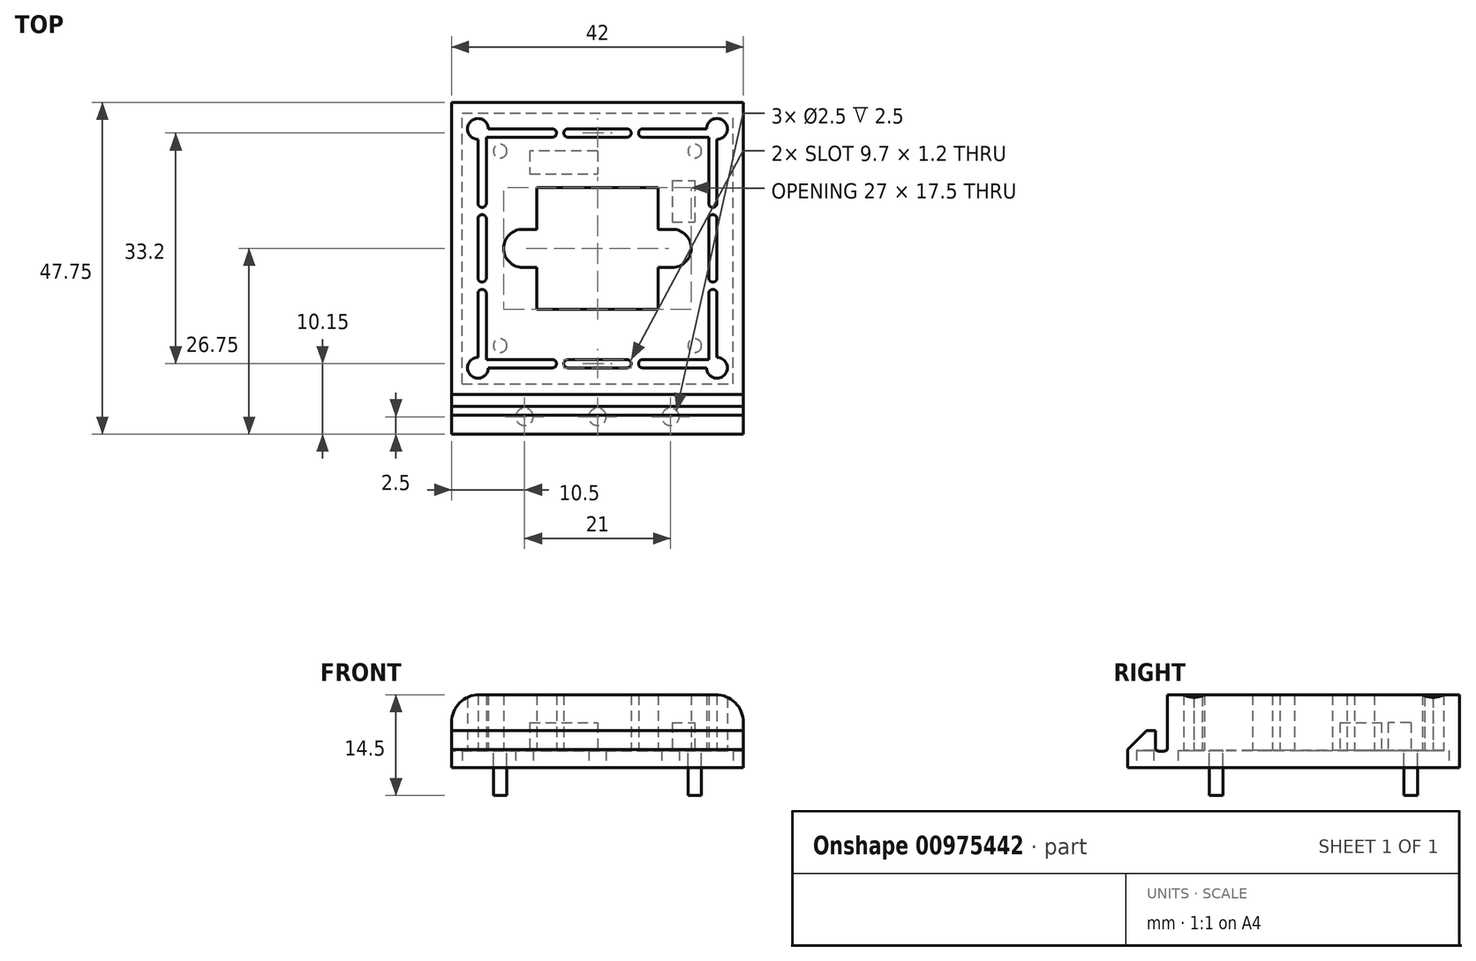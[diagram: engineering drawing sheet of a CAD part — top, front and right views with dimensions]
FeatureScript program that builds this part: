
annotation { "Feature Type Name" : "Feature", "Feature Type Description" : "" }
export const myFeature = defineFeature(function(context is Context, id is Id, definition is map)
    precondition{}
    {
        {
            var Q0;
            Q0=qCreatedBy(makeId("Top.planeOp"),FACE);
            var sketch = newSketch(context, id + "F0", { "sketchPlane" : qUnion([Q0])});
            skLineSegment(sketch, "E0.bottom", {"start": v(19, 19) * mm, "end": v(-19, 19) * mm, "construction": true});
            skLineSegment(sketch, "E0.top", {"start": v(19, -19) * mm, "end": v(-19, -19) * mm, "construction": true});
            skLineSegment(sketch, "E0.left", {"start": v(19, 19) * mm, "end": v(19, -19) * mm, "construction": true});
            skLineSegment(sketch, "E0.right", {"start": v(-19, 19) * mm, "end": v(-19, -19) * mm, "construction": true});
            skPoint(sketch, "E0.middle", {"position": v(0, 0) * mm});
            skPoint(sketch, "E1", {"position": v(19, 0) * mm});
            skPoint(sketch, "E2", {"position": v(-19, 0) * mm});
            skPoint(sketch, "E3", {"position": v(0, 19) * mm});
            skPoint(sketch, "E4", {"position": v(0, -19) * mm});
            skPoint(sketch, "E5", {"position": v(17.2, 0) * mm});
            skPoint(sketch, "E6", {"position": v(-17.2, 0) * mm});
            skLineSegment(sketch, "E7", {"start": v(-19, 0) * mm, "end": v(-17.2, 0) * mm, "construction": true});
            skLineSegment(sketch, "E8", {"start": v(19, 0) * mm, "end": v(17.2, 0) * mm, "construction": true});
            skLineSegment(sketch, "E9", {"start": v(0, 19) * mm, "end": v(0, 17.2) * mm, "construction": true});
            skLineSegment(sketch, "E10", {"start": v(0, -17.2) * mm, "end": v(0, -19) * mm, "construction": true});
            skPoint(sketch, "E11", {"position": v(-16, 16) * mm});
            skPoint(sketch, "E12", {"position": v(16, -16) * mm});
            skPoint(sketch, "E13", {"position": v(16, 16) * mm});
            skPoint(sketch, "E14", {"position": v(-16, -16) * mm});
            skPoint(sketch, "E15", {"position": v(17.2, 4.25) * mm});
            skPoint(sketch, "E16", {"position": v(17.2, -4.25) * mm});
            skPoint(sketch, "E17", {"position": v(16, -4.25) * mm});
            skPoint(sketch, "E18", {"position": v(16, 4.25) * mm});
            skPoint(sketch, "E19", {"position": v(-17.2, 4.25) * mm});
            skPoint(sketch, "E20", {"position": v(-16, 4.25) * mm});
            skPoint(sketch, "E21", {"position": v(-17.2, -4.25) * mm});
            skPoint(sketch, "E22", {"position": v(-16, -4.25) * mm});
            skPoint(sketch, "E23", {"position": v(-4.25, 17.2) * mm});
            skPoint(sketch, "E24", {"position": v(-4.25, 16) * mm});
            skPoint(sketch, "E25", {"position": v(4.25, 17.2) * mm});
            skPoint(sketch, "E26", {"position": v(4.25, 16) * mm});
            skPoint(sketch, "E27", {"position": v(-4.25, -16) * mm});
            skPoint(sketch, "E28", {"position": v(4.25, -16) * mm});
            skPoint(sketch, "E29", {"position": v(-4.25, -17.2) * mm});
            skPoint(sketch, "E30", {"position": v(4.25, -17.2) * mm});
            skLineSegment(sketch, "E31", {"start": v(17.2, 4.25) * mm, "end": v(17.2, -4.25) * mm});
            skLineSegment(sketch, "E32", {"start": v(16, 4.25) * mm, "end": v(16, -4.25) * mm});
            skLineSegment(sketch, "E33", {"start": v(4.25, 16) * mm, "end": v(-4.25, 16) * mm});
            skLineSegment(sketch, "E34", {"start": v(-4.25, 17.2) * mm, "end": v(4.25, 17.2) * mm});
            skLineSegment(sketch, "E35", {"start": v(-16, 4.25) * mm, "end": v(-16, -4.25) * mm});
            skLineSegment(sketch, "E36", {"start": v(-17.2, -4.25) * mm, "end": v(-17.2, 4.25) * mm});
            skLineSegment(sketch, "E37", {"start": v(-4.25, -16) * mm, "end": v(4.25, -16) * mm});
            skLineSegment(sketch, "E38", {"start": v(4.25, -17.2) * mm, "end": v(-4.25, -17.2) * mm});
            skArc(sketch, "E39", {"start": v(16, 4.25) * mm, "mid": v(16.6, 4.85) * mm, "end": v(17.2, 4.25) * mm});
            skArc(sketch, "E40", {"start": v(17.2, -4.25) * mm, "mid": v(16.6, -4.85) * mm, "end": v(16, -4.25) * mm});
            skArc(sketch, "E41", {"start": v(4.25, -16) * mm, "mid": v(4.85, -16.6) * mm, "end": v(4.25, -17.2) * mm});
            skArc(sketch, "E42", {"start": v(-4.25, -16) * mm, "mid": v(-4.85, -16.6) * mm, "end": v(-4.25, -17.2) * mm});
            skArc(sketch, "E43", {"start": v(-17.2, -4.25) * mm, "mid": v(-16.6, -4.85) * mm, "end": v(-16, -4.25) * mm});
            skArc(sketch, "E44", {"start": v(-17.2, 4.25) * mm, "mid": v(-16.6, 4.85) * mm, "end": v(-16, 4.25) * mm});
            skArc(sketch, "E45", {"start": v(-4.25, 16) * mm, "mid": v(-4.85, 16.6) * mm, "end": v(-4.25, 17.2) * mm});
            skArc(sketch, "E46", {"start": v(4.25, 16) * mm, "mid": v(4.85, 16.6) * mm, "end": v(4.25, 17.2) * mm});
            skPoint(sketch, "E47", {"position": v(-6.5, 16) * mm});
            skPoint(sketch, "E48", {"position": v(-6.5, 17.2) * mm});
            skPoint(sketch, "E49", {"position": v(-16, 6.5) * mm});
            skPoint(sketch, "E50", {"position": v(-17.2, 6.5) * mm});
            skPoint(sketch, "E51", {"position": v(6.5, 16) * mm});
            skPoint(sketch, "E52", {"position": v(6.5, 17.2) * mm});
            skPoint(sketch, "E53", {"position": v(16, 6.5) * mm});
            skPoint(sketch, "E54", {"position": v(17.2, 6.5) * mm});
            skPoint(sketch, "E55", {"position": v(-17.2, -6.5) * mm});
            skPoint(sketch, "E56", {"position": v(-16, -6.5) * mm});
            skPoint(sketch, "E57", {"position": v(17.2, -6.5) * mm});
            skPoint(sketch, "E58", {"position": v(16, -6.5) * mm});
            skPoint(sketch, "E59", {"position": v(6.5, -17.2) * mm});
            skPoint(sketch, "E60", {"position": v(6.5, -16) * mm});
            skPoint(sketch, "E61", {"position": v(-6.5, -17.2) * mm});
            skPoint(sketch, "E62", {"position": v(-6.5, -16) * mm});
            skLineSegment(sketch, "E63", {"start": v(-6.5, 17.2) * mm, "end": v(-6.5, 16) * mm, "construction": true});
            skLineSegment(sketch, "E64", {"start": v(-17.2, 6.5) * mm, "end": v(-16, 6.5) * mm, "construction": true});
            skLineSegment(sketch, "E65", {"start": v(6.5, 17.2) * mm, "end": v(6.5, 16) * mm, "construction": true});
            skLineSegment(sketch, "E66", {"start": v(16, 6.5) * mm, "end": v(17.2, 6.5) * mm, "construction": true});
            skLineSegment(sketch, "E67", {"start": v(-17.2, -6.5) * mm, "end": v(-16, -6.5) * mm, "construction": true});
            skLineSegment(sketch, "E68", {"start": v(-6.5, -16) * mm, "end": v(-6.5, -17.2) * mm, "construction": true});
            skLineSegment(sketch, "E69", {"start": v(16, -6.5) * mm, "end": v(17.2, -6.5) * mm, "construction": true});
            skLineSegment(sketch, "E70", {"start": v(6.5, -16) * mm, "end": v(6.5, -17.2) * mm, "construction": true});
            skArc(sketch, "E71", {"start": v(-6.5, 17.2) * mm, "mid": v(-5.9, 16.6) * mm, "end": v(-6.5, 16) * mm});
            skArc(sketch, "E72", {"start": v(-16, 6.5) * mm, "mid": v(-16.6, 5.9) * mm, "end": v(-17.2, 6.5) * mm});
            skArc(sketch, "E73", {"start": v(6.5, 17.2) * mm, "mid": v(5.9, 16.6) * mm, "end": v(6.5, 16) * mm});
            skArc(sketch, "E74", {"start": v(17.2, 6.5) * mm, "mid": v(16.6, 5.9) * mm, "end": v(16, 6.5) * mm});
            skArc(sketch, "E75", {"start": v(-16, -6.5) * mm, "mid": v(-16.6, -5.9) * mm, "end": v(-17.2, -6.5) * mm});
            skArc(sketch, "E76", {"start": v(-6.5, -16) * mm, "mid": v(-5.9, -16.6) * mm, "end": v(-6.5, -17.2) * mm});
            skArc(sketch, "E77", {"start": v(6.5, -16) * mm, "mid": v(5.9, -16.6) * mm, "end": v(6.5, -17.2) * mm});
            skArc(sketch, "E78", {"start": v(17.2, -6.5) * mm, "mid": v(16.6, -5.9) * mm, "end": v(16, -6.5) * mm});
            skLineSegment(sketch, "E79", {"start": v(6.5, 17.2) * mm, "end": v(16, 17.2) * mm});
            skLineSegment(sketch, "E80", {"start": v(6.5, 16) * mm, "end": v(16, 16) * mm});
            skLineSegment(sketch, "E81", {"start": v(16, 6.5) * mm, "end": v(16, 16) * mm});
            skLineSegment(sketch, "E82", {"start": v(17.2, 16) * mm, "end": v(17.2, 6.5) * mm});
            skLineSegment(sketch, "E83", {"start": v(-16, 17.2) * mm, "end": v(-6.5, 17.2) * mm});
            skLineSegment(sketch, "E84", {"start": v(-16, 16) * mm, "end": v(-6.5, 16) * mm});
            skLineSegment(sketch, "E85", {"start": v(-16, 16) * mm, "end": v(-16, 6.5) * mm});
            skLineSegment(sketch, "E86", {"start": v(-17.2, 6.5) * mm, "end": v(-17.2, 16) * mm});
            skLineSegment(sketch, "E87", {"start": v(-16, -6.5) * mm, "end": v(-16, -16) * mm});
            skLineSegment(sketch, "E88", {"start": v(-6.5, -16) * mm, "end": v(-16, -16) * mm});
            skLineSegment(sketch, "E89", {"start": v(-17.2, -6.5) * mm, "end": v(-17.2, -16) * mm});
            skLineSegment(sketch, "E90", {"start": v(-16, -17.2) * mm, "end": v(-6.5, -17.2) * mm});
            skLineSegment(sketch, "E91", {"start": v(6.5, -17.2) * mm, "end": v(16, -17.2) * mm});
            skLineSegment(sketch, "E92", {"start": v(6.5, -16) * mm, "end": v(16, -16) * mm});
            skLineSegment(sketch, "E93", {"start": v(17.2, -16) * mm, "end": v(17.2, -6.5) * mm});
            skLineSegment(sketch, "E94", {"start": v(16, -6.5) * mm, "end": v(16, -16) * mm});
            skLineSegment(sketch, "E95", {"start": v(-17.2, 6.5) * mm, "end": v(-19, 6.5) * mm, "construction": true});
            skLineSegment(sketch, "E96", {"start": v(-17.2, -6.5) * mm, "end": v(-19, -6.5) * mm, "construction": true});
            skLineSegment(sketch, "E97", {"start": v(-6.5, 17.2) * mm, "end": v(-6.5, 19) * mm, "construction": true});
            skLineSegment(sketch, "E98", {"start": v(-6.5, -17.2) * mm, "end": v(-6.5, -19) * mm, "construction": true});
            skLineSegment(sketch, "E99", {"start": v(6.5, -17.2) * mm, "end": v(6.5, -19) * mm, "construction": true});
            skLineSegment(sketch, "E100", {"start": v(17.2, -6.5) * mm, "end": v(19, -6.5) * mm, "construction": true});
            skLineSegment(sketch, "E101", {"start": v(17.2, 6.5) * mm, "end": v(19, 6.5) * mm, "construction": true});
            skLineSegment(sketch, "E102", {"start": v(6.5, 17.2) * mm, "end": v(6.5, 19) * mm, "construction": true});
            skPoint(sketch, "E103", {"position": v(-11.25, 17.2) * mm});
            skPoint(sketch, "E104", {"position": v(-11.25, 16) * mm});
            skPoint(sketch, "E105", {"position": v(-17.2, 11.25) * mm});
            skPoint(sketch, "E106", {"position": v(-16, 11.25) * mm});
            skPoint(sketch, "E107", {"position": v(11.25, 17.2) * mm});
            skPoint(sketch, "E108", {"position": v(11.25, 16) * mm});
            skPoint(sketch, "E109", {"position": v(16, 11.25) * mm});
            skPoint(sketch, "E110", {"position": v(17.2, 11.25) * mm});
            skPoint(sketch, "E111", {"position": v(16, -11.25) * mm});
            skPoint(sketch, "E112", {"position": v(17.2, -11.25) * mm});
            skPoint(sketch, "E113", {"position": v(11.25, -16) * mm});
            skPoint(sketch, "E114", {"position": v(11.25, -17.2) * mm});
            skPoint(sketch, "E115", {"position": v(-11.25, -16) * mm});
            skPoint(sketch, "E116", {"position": v(-11.25, -17.2) * mm});
            skPoint(sketch, "E117", {"position": v(-16, -11.25) * mm});
            skPoint(sketch, "E118", {"position": v(-17.2, -11.25) * mm});
            skLineSegment(sketch, "E119", {"start": v(-17.2, 11.25) * mm, "end": v(-16, 11.25) * mm, "construction": true});
            skLineSegment(sketch, "E120", {"start": v(-11.25, 17.2) * mm, "end": v(-11.25, 16) * mm, "construction": true});
            skLineSegment(sketch, "E121", {"start": v(-11.25, -16) * mm, "end": v(-11.25, -17.2) * mm, "construction": true});
            skLineSegment(sketch, "E122", {"start": v(-16, -11.25) * mm, "end": v(-17.2, -11.25) * mm, "construction": true});
            skLineSegment(sketch, "E123", {"start": v(11.25, 17.2) * mm, "end": v(11.25, 16) * mm, "construction": true});
            skLineSegment(sketch, "E124", {"start": v(16, 11.25) * mm, "end": v(17.2, 11.25) * mm, "construction": true});
            skLineSegment(sketch, "E125", {"start": v(11.25, -17.2) * mm, "end": v(11.25, -16) * mm, "construction": true});
            skLineSegment(sketch, "E126", {"start": v(16, -11.25) * mm, "end": v(17.2, -11.25) * mm, "construction": true});
            skPoint(sketch, "E127", {"position": v(-14, 14) * mm});
            skLineSegment(sketch, "E128", {"start": v(-14, 19) * mm, "end": v(-14, 14) * mm, "construction": true});
            skLineSegment(sketch, "E129", {"start": v(-14, 14) * mm, "end": v(-19, 14) * mm, "construction": true});
            skPoint(sketch, "E130", {"position": v(-14, -14) * mm});
            skLineSegment(sketch, "E131", {"start": v(-19, -14) * mm, "end": v(-14, -14) * mm, "construction": true});
            skLineSegment(sketch, "E132", {"start": v(-14, -19) * mm, "end": v(-14, -14) * mm, "construction": true});
            skPoint(sketch, "E133", {"position": v(14, -14) * mm});
            skLineSegment(sketch, "E134", {"start": v(14, -19) * mm, "end": v(14, -14) * mm, "construction": true});
            skLineSegment(sketch, "E135", {"start": v(14, -14) * mm, "end": v(19, -14) * mm, "construction": true});
            skPoint(sketch, "E136", {"position": v(14, 14) * mm});
            skLineSegment(sketch, "E137", {"start": v(14, 19) * mm, "end": v(14, 14) * mm, "construction": true});
            skLineSegment(sketch, "E138", {"start": v(19, 14) * mm, "end": v(14, 14) * mm, "construction": true});
            skPoint(sketch, "E139", {"position": v(16, 0) * mm});
            skPoint(sketch, "E140", {"position": v(0, 16) * mm});
            skPoint(sketch, "E141", {"position": v(-16, 0) * mm});
            skPoint(sketch, "E142", {"position": v(0, -16) * mm});
            skLineSegment(sketch, "E143", {"start": v(16, 0) * mm, "end": v(17.2, 0) * mm, "construction": true});
            skLineSegment(sketch, "E144", {"start": v(0, 17.2) * mm, "end": v(0, 16) * mm, "construction": true});
            skLineSegment(sketch, "E145", {"start": v(0, -16) * mm, "end": v(0, -17.2) * mm, "construction": true});
            skLineSegment(sketch, "E146", {"start": v(-17.2, 0) * mm, "end": v(-16, 0) * mm, "construction": true});
            skPoint(sketch, "E147", {"position": v(-17.2, 17.2) * mm});
            skPoint(sketch, "E148", {"position": v(17.2, 17.2) * mm});
            skPoint(sketch, "E149", {"position": v(-17.2, -17.2) * mm});
            skPoint(sketch, "E150", {"position": v(17.2, -17.2) * mm});
            skLineSegment(sketch, "E151", {"start": v(16, 4.25) * mm, "end": v(17.2, 4.25) * mm, "construction": true});
            skLineSegment(sketch, "E152", {"start": v(16, -4.25) * mm, "end": v(17.2, -4.25) * mm, "construction": true});
            skLineSegment(sketch, "E153", {"start": v(-4.25, 16) * mm, "end": v(-4.25, 17.2) * mm, "construction": true});
            skLineSegment(sketch, "E154", {"start": v(4.25, 16) * mm, "end": v(4.25, 17.2) * mm, "construction": true});
            skLineSegment(sketch, "E155", {"start": v(-16, 4.25) * mm, "end": v(-17.2, 4.25) * mm, "construction": true});
            skLineSegment(sketch, "E156", {"start": v(-16, -4.25) * mm, "end": v(-17.2, -4.25) * mm, "construction": true});
            skLineSegment(sketch, "E157", {"start": v(-4.25, -16) * mm, "end": v(-4.25, -17.2) * mm, "construction": true});
            skLineSegment(sketch, "E158", {"start": v(4.25, -16) * mm, "end": v(4.25, -17.2) * mm, "construction": true});
            skLineSegment(sketch, "E159", {"start": v(-6.5, 17.2) * mm, "end": v(-4.25, 17.2) * mm, "construction": true});
            skLineSegment(sketch, "E160", {"start": v(4.25, 17.2) * mm, "end": v(6.5, 17.2) * mm, "construction": true});
            skLineSegment(sketch, "E161", {"start": v(17.2, 6.5) * mm, "end": v(17.2, 4.25) * mm, "construction": true});
            skLineSegment(sketch, "E162", {"start": v(17.2, -6.5) * mm, "end": v(17.2, -4.25) * mm, "construction": true});
            skLineSegment(sketch, "E163", {"start": v(6.5, -17.2) * mm, "end": v(4.25, -17.2) * mm, "construction": true});
            skLineSegment(sketch, "E164", {"start": v(-4.25, -17.2) * mm, "end": v(-6.5, -17.2) * mm, "construction": true});
            skLineSegment(sketch, "E165", {"start": v(-17.2, -6.5) * mm, "end": v(-17.2, -4.25) * mm, "construction": true});
            skLineSegment(sketch, "E166", {"start": v(-17.2, 4.25) * mm, "end": v(-17.2, 6.5) * mm, "construction": true});
            skCircle(sketch, "E167", {"center": v(14, 14) * mm, "radius": 0.97 * mm});
            skPoint(sketch, "E168", {"position": v(14, 14.97) * mm});
            skPoint(sketch, "E169", {"position": v(14.97, 14) * mm});
            skPoint(sketch, "E170", {"position": v(16, 14) * mm});
            skPoint(sketch, "E171", {"position": v(14, 16) * mm});
            skCircle(sketch, "E172", {"center": v(-14, 14) * mm, "radius": 0.97 * mm});
            skPoint(sketch, "E173", {"position": v(-14, 14.97) * mm});
            skPoint(sketch, "E174", {"position": v(-14.97, 14) * mm});
            skCircle(sketch, "E175", {"center": v(-14, -14) * mm, "radius": 0.97 * mm});
            skCircle(sketch, "E176", {"center": v(14, -14) * mm, "radius": 0.97 * mm});
            skPoint(sketch, "E177", {"position": v(14, -14.97) * mm});
            skPoint(sketch, "E178", {"position": v(14.97, -14) * mm});
            skPoint(sketch, "E179", {"position": v(-14.97, -14) * mm});
            skPoint(sketch, "E180", {"position": v(-14, -14.97) * mm});
            skLineSegment(sketch, "E181.bottom", {"start": v(8.75, 8.75) * mm, "end": v(-8.75, 8.75) * mm});
            skLineSegment(sketch, "E181.top", {"start": v(8.75, -8.75) * mm, "end": v(-8.75, -8.75) * mm});
            skLineSegment(sketch, "E181.left", {"start": v(8.75, 8.75) * mm, "end": v(8.75, 2.75) * mm});
            skLineSegment(sketch, "E181.right", {"start": v(-8.75, 8.75) * mm, "end": v(-8.75, 2.75) * mm});
            skLineSegment(sketch, "E182.bottom", {"start": v(-21, 21) * mm, "end": v(-2.62, 21) * mm});
            skLineSegment(sketch, "E182.top", {"start": v(-21, -21) * mm, "end": v(-2.63, -21) * mm});
            skLineSegment(sketch, "E182.left", {"start": v(-21, 21) * mm, "end": v(-21, -21) * mm});
            skLineSegment(sketch, "E182.right", {"start": v(21, 21) * mm, "end": v(21, -21) * mm});
            skPoint(sketch, "E183", {"position": v(0, 21) * mm});
            skPoint(sketch, "E184", {"position": v(-2.62, 21) * mm});
            skPoint(sketch, "E185", {"position": v(2.62, 21) * mm});
            skLineSegment(sketch, "E186.trimOffspring", {"start": v(2.62, 21) * mm, "end": v(21, 21) * mm});
            skPoint(sketch, "E187", {"position": v(0, -21) * mm});
            skPoint(sketch, "E188", {"position": v(-2.63, -21) * mm});
            skPoint(sketch, "E189", {"position": v(2.63, -21) * mm});
            skLineSegment(sketch, "E190.trimOffspring", {"start": v(2.63, -21) * mm, "end": v(21, -21) * mm});
            skLineSegment(sketch, "E191", {"start": v(-2.62, 21) * mm, "end": v(2.63, 21) * mm});
            skLineSegment(sketch, "E192", {"start": v(-2.63, -21) * mm, "end": v(2.63, -21) * mm});
            skPoint(sketch, "E193", {"position": v(-8.75, 0) * mm});
            skPoint(sketch, "E194", {"position": v(8.75, 0) * mm});
            skPoint(sketch, "E195", {"position": v(8.75, -2.75) * mm});
            skPoint(sketch, "E196", {"position": v(8.75, 2.75) * mm});
            skPoint(sketch, "E197", {"position": v(-8.75, -2.75) * mm});
            skPoint(sketch, "E198", {"position": v(-8.75, 2.75) * mm});
            skLineSegment(sketch, "E199", {"start": v(-8.75, -2.75) * mm, "end": v(8.75, -2.75) * mm, "construction": true});
            skLineSegment(sketch, "E200", {"start": v(8.75, 2.75) * mm, "end": v(-8.75, 2.75) * mm, "construction": true});
            skPoint(sketch, "E201", {"position": v(10.75, 0) * mm});
            skPoint(sketch, "E202", {"position": v(-10.75, 0) * mm});
            skLineSegment(sketch, "E203", {"start": v(10.75, 0) * mm, "end": v(8.75, 0) * mm, "construction": true});
            skLineSegment(sketch, "E204", {"start": v(-10.75, 0) * mm, "end": v(-8.75, 0) * mm, "construction": true});
            skLineSegment(sketch, "E205", {"start": v(-8.75, -2.75) * mm, "end": v(-10.75, -2.75) * mm});
            skLineSegment(sketch, "E206", {"start": v(-8.75, 2.75) * mm, "end": v(-10.75, 2.75) * mm});
            skLineSegment(sketch, "E207", {"start": v(8.75, -2.75) * mm, "end": v(10.75, -2.75) * mm});
            skLineSegment(sketch, "E208", {"start": v(8.75, 2.75) * mm, "end": v(10.75, 2.75) * mm});
            skArc(sketch, "E209", {"start": v(-10.75, 2.75) * mm, "mid": v(-13.5, 0) * mm, "end": v(-10.75, -2.75) * mm});
            skArc(sketch, "E210", {"start": v(10.75, -2.75) * mm, "mid": v(13.5, 0) * mm, "end": v(10.75, 2.75) * mm});
            skLineSegment(sketch, "E211.trimOffspring", {"start": v(-8.75, -2.75) * mm, "end": v(-8.75, -8.75) * mm});
            skLineSegment(sketch, "E212.trimOffspring", {"start": v(8.75, -2.75) * mm, "end": v(8.75, -8.75) * mm});
            skLineSegment(sketch, "E213", {"start": v(-16, -6.5) * mm, "end": v(-16, -4.25) * mm});
            skLineSegment(sketch, "E214", {"start": v(-16, 4.25) * mm, "end": v(-16, 6.5) * mm});
            skLineSegment(sketch, "E215", {"start": v(-6.5, -16) * mm, "end": v(-4.25, -16) * mm});
            skLineSegment(sketch, "E216", {"start": v(4.25, -16) * mm, "end": v(6.5, -16) * mm});
            skLineSegment(sketch, "E217", {"start": v(16, -4.25) * mm, "end": v(16, -6.5) * mm});
            skLineSegment(sketch, "E218", {"start": v(16, 4.25) * mm, "end": v(16, 6.5) * mm});
            skLineSegment(sketch, "E219", {"start": v(6.5, 16) * mm, "end": v(4.25, 16) * mm});
            skLineSegment(sketch, "E220", {"start": v(-4.25, 16) * mm, "end": v(-6.5, 16) * mm});
            skArc(sketch, "E221", {"start": v(-15.7, 17.2) * mm, "mid": v(-18.26, 18.26) * mm, "end": v(-17.2, 15.7) * mm});
            skLineSegment(sketch, "E222", {"start": v(-17.2, 16) * mm, "end": v(-17.2, 17.2) * mm, "construction": true});
            skLineSegment(sketch, "E223", {"start": v(-17.2, 17.2) * mm, "end": v(-17.2, 19) * mm, "construction": true});
            skLineSegment(sketch, "E224", {"start": v(-16, 17.2) * mm, "end": v(-17.2, 17.2) * mm, "construction": true});
            skLineSegment(sketch, "E225", {"start": v(-17.2, 17.2) * mm, "end": v(-19, 17.2) * mm, "construction": true});
            skArc(sketch, "E226", {"start": v(17.2, 15.7) * mm, "mid": v(18.26, 18.26) * mm, "end": v(15.7, 17.2) * mm});
            skLineSegment(sketch, "E227", {"start": v(16, 17.2) * mm, "end": v(17.2, 17.2) * mm, "construction": true});
            skLineSegment(sketch, "E228", {"start": v(17.2, 16) * mm, "end": v(17.2, 17.2) * mm, "construction": true});
            skLineSegment(sketch, "E229", {"start": v(17.2, 17.2) * mm, "end": v(17.2, 19) * mm, "construction": true});
            skLineSegment(sketch, "E230", {"start": v(17.2, 17.2) * mm, "end": v(19, 17.2) * mm, "construction": true});
            skArc(sketch, "E231", {"start": v(-17.2, -15.7) * mm, "mid": v(-18.26, -18.26) * mm, "end": v(-15.7, -17.2) * mm});
            skArc(sketch, "E232", {"start": v(15.7, -17.2) * mm, "mid": v(18.26, -18.26) * mm, "end": v(17.2, -15.7) * mm});
            skLineSegment(sketch, "E233", {"start": v(17.2, -16) * mm, "end": v(17.2, -17.2) * mm, "construction": true});
            skLineSegment(sketch, "E234", {"start": v(17.2, -17.2) * mm, "end": v(17.2, -19) * mm, "construction": true});
            skLineSegment(sketch, "E235", {"start": v(16, -17.2) * mm, "end": v(17.2, -17.2) * mm, "construction": true});
            skLineSegment(sketch, "E236", {"start": v(17.2, -17.2) * mm, "end": v(19, -17.2) * mm, "construction": true});
            skLineSegment(sketch, "E237", {"start": v(-17.2, -16) * mm, "end": v(-17.2, -17.2) * mm, "construction": true});
            skLineSegment(sketch, "E238", {"start": v(-17.2, -17.2) * mm, "end": v(-17.2, -19) * mm, "construction": true});
            skLineSegment(sketch, "E239", {"start": v(-16, -17.2) * mm, "end": v(-17.2, -17.2) * mm, "construction": true});
            skLineSegment(sketch, "E240", {"start": v(-17.2, -17.2) * mm, "end": v(-19, -17.2) * mm, "construction": true});
            skPoint(sketch, "E241", {"position": v(15.7, 17.2) * mm});
            skPoint(sketch, "E242", {"position": v(17.2, 15.7) * mm});
            skPoint(sketch, "E243", {"position": v(-17.2, 15.7) * mm});
            skPoint(sketch, "E244", {"position": v(-15.7, 17.2) * mm});
            skPoint(sketch, "E245", {"position": v(-17.2, -15.7) * mm});
            skPoint(sketch, "E246", {"position": v(-15.7, -17.2) * mm});
            skPoint(sketch, "E247", {"position": v(15.7, -17.2) * mm});
            skPoint(sketch, "E248", {"position": v(17.2, -15.7) * mm});
            skLineSegment(sketch, "E249.bottom", {"start": v(-19.5, -19.5) * mm, "end": v(19.5, -19.5) * mm});
            skLineSegment(sketch, "E249.top", {"start": v(-19.5, 19.5) * mm, "end": v(19.5, 19.5) * mm});
            skLineSegment(sketch, "E249.left", {"start": v(-19.5, -19.5) * mm, "end": v(-19.5, 19.5) * mm});
            skLineSegment(sketch, "E249.right", {"start": v(19.5, -19.5) * mm, "end": v(19.5, 19.5) * mm});
            skPoint(sketch, "E250", {"position": v(-8.75, 10.75) * mm});
            skPoint(sketch, "E251", {"position": v(-8.75, 14) * mm});
            skPoint(sketch, "E252", {"position": v(0, 8.75) * mm});
            skPoint(sketch, "E253", {"position": v(0, 10.75) * mm});
            skPoint(sketch, "E254", {"position": v(0, 14) * mm});
            skLineSegment(sketch, "E255", {"start": v(0, 14) * mm, "end": v(0, 10.75) * mm});
            skLineSegment(sketch, "E256", {"start": v(-8.75, 10.75) * mm, "end": v(0, 10.75) * mm});
            skLineSegment(sketch, "E257", {"start": v(0, 14) * mm, "end": v(-8.75, 14) * mm});
            skLineSegment(sketch, "E258", {"start": v(-8.75, 14) * mm, "end": v(-9.75, 14) * mm});
            skLineSegment(sketch, "E259", {"start": v(-9.75, 14) * mm, "end": v(-9.75, 10.75) * mm});
            skLineSegment(sketch, "E260", {"start": v(-9.75, 10.75) * mm, "end": v(-8.75, 10.75) * mm});
            skPoint(sketch, "E261", {"position": v(10.75, 8.75) * mm});
            skPoint(sketch, "E262", {"position": v(14, 8.75) * mm});
            skLineSegment(sketch, "E263", {"start": v(10.75, 8.75) * mm, "end": v(10.75, 3.81) * mm});
            skLineSegment(sketch, "E264", {"start": v(10.75, 3.81) * mm, "end": v(14, 3.81) * mm});
            skLineSegment(sketch, "E265", {"start": v(14, 3.81) * mm, "end": v(14, 8.75) * mm});
            skLineSegment(sketch, "E266", {"start": v(10.75, 8.75) * mm, "end": v(10.75, 9.75) * mm});
            skLineSegment(sketch, "E267", {"start": v(10.75, 9.75) * mm, "end": v(14, 9.75) * mm});
            skLineSegment(sketch, "E268", {"start": v(14, 9.75) * mm, "end": v(14, 8.75) * mm});
            skSolve(sketch);
        }
        {
            var Q0;
            Q0=qSketchRegion(id+"F0",true);
            var Q1;
            Q1=makeQuery(id+"F0.imprint","IMPRINT",FACE,{"disambiguationData":[TD([[makeQuery(id+"F0.imprint","IMPRINT",EDGE,{"derivedFrom":sQuery(id+"F0.wireOp",EDGE,"E176")}),1.0]])]});
            var Q2;
            Q2=makeQuery(id+"F0.imprint","IMPRINT",FACE,{"disambiguationData":[TD([[makeQuery(id+"F0.imprint","IMPRINT",EDGE,{"derivedFrom":sQuery(id+"F0.wireOp",EDGE,"E175")}),1.0]])]});
            var Q3;
            Q3=makeQuery(id+"F0.imprint","IMPRINT",FACE,{"disambiguationData":[TD([[makeQuery(id+"F0.imprint","IMPRINT",EDGE,{"derivedFrom":sQuery(id+"F0.wireOp",EDGE,"E172")}),1.0]])]});
            var Q4;
            Q4=makeQuery(id+"F0.imprint","IMPRINT",FACE,{"disambiguationData":[TD([[makeQuery(id+"F0.imprint","IMPRINT",EDGE,{"derivedFrom":sQuery(id+"F0.wireOp",EDGE,"E167")}),1.0]])]});
            var Q5;
            Q5=makeQuery(id+"F0.imprint","IMPRINT",FACE,{"disambiguationData":[TD([[makeQuery(id+"F0.imprint","IMPRINT",EDGE,{"derivedFrom":sQuery(id+"F0.wireOp",EDGE,"E32")}),-1.0]])]});
            var Q6;
            Q6=makeQuery(id+"F0.imprint","IMPRINT",FACE,{"disambiguationData":[TD([[makeQuery(id+"F0.imprint","IMPRINT",EDGE,{"derivedFrom":sQuery(id+"F0.wireOp",EDGE,"E31")}),1.0]])]});
            var Q7;
            Q7=makeQuery(id+"F0.imprint","IMPRINT",FACE,{"disambiguationData":[TD([[makeQuery(id+"F0.imprint","IMPRINT",EDGE,{"derivedFrom":sQuery(id+"F0.wireOp",EDGE,"E263")}),1.0]])]});
            var Q8;
            Q8=makeQuery(id+"F0.imprint","IMPRINT",FACE,{"disambiguationData":[TD([[makeQuery(id+"F0.imprint","IMPRINT",EDGE,{"derivedFrom":sQuery(id+"F0.wireOp",EDGE,"E255")}),-1.0]])]});
            extrude(context, id + "F1", {"entities" : qUnion([Q0, Q1, Q2, Q3, Q4, Q5, Q6, Q7, Q8]), "depth" : 9 * mm, "offsetDistance" : 25 * mm});
        }
        {
            var Q0;
            Q0=makeQuery(id+"F1.opExtrude","CAP_EDGE",EDGE,{"disambiguationData":[OSD([sQuery(id+"F0.wireOp",EDGE,"E182.left")])],"isStart":false});
            var Q1;
            Q1=makeQuery(id+"F1.opExtrude","CAP_EDGE",EDGE,{"disambiguationData":[OSD([sQuery(id+"F0.wireOp",EDGE,"E182.right")])],"isStart":false});
            fillet(context, id + "F2", {"entities" : qUnion([Q0, Q1]), "radius" : 4 * mm, "tangentPropagation" : true, "allowEdgeOverflow" : false});
        }
        {
            var Q0;
            Q0=qCreatedBy(makeId("Right.planeOp"),FACE);
            var sketch = newSketch(context, id + "F3", { "sketchPlane" : qUnion([Q0])});
            skLineSegment(sketch, "E269", {"start": v(-21, 1.1) * mm, "end": v(-21, 0) * mm});
            skLineSegment(sketch, "E270", {"start": v(-21, 0) * mm, "end": v(-21, -1.5) * mm});
            skLineSegment(sketch, "E271", {"start": v(-21, -1.5) * mm, "end": v(-22.75, -1.5) * mm});
            skLineSegment(sketch, "E272", {"start": v(-21, 1.1) * mm, "end": v(-22.75, 1.1) * mm, "construction": true});
            skLineSegment(sketch, "E273", {"start": v(-22.75, 1.1) * mm, "end": v(-22.75, -1.5) * mm, "construction": true});
            skLineSegment(sketch, "E274", {"start": v(-22.75, 1.1) * mm, "end": v(-22.75, 3.85) * mm});
            skLineSegment(sketch, "E275", {"start": v(-22.75, 3.85) * mm, "end": v(-24, 3.85) * mm});
            skLineSegment(sketch, "E276", {"start": v(-24, 3.85) * mm, "end": v(-26.75, 1.1) * mm});
            skLineSegment(sketch, "E277", {"start": v(-26.75, 1.1) * mm, "end": v(-26.75, -1.5) * mm});
            skLineSegment(sketch, "E278", {"start": v(-26.75, -1.5) * mm, "end": v(-22.75, -1.5) * mm});
            skArc(sketch, "E279", {"start": v(-22.75, 1.1) * mm, "mid": v(-21.88, 0.82) * mm, "end": v(-21, 1.1) * mm});
            skSolve(sketch);
        }
        {
            var Q0;
            Q0=qSketchRegion(id+"F3",true);
            extrude(context, id + "F4", {"entities" : qUnion([Q0]), "operationType" : NewBodyOperationType.ADD, "depth" : 21 * mm, "offsetDistance" : 25 * mm});
        }
        {
            var Q0;
            Q0=makeQuery(id+"F4.opExtrude","CAP_FACE",FACE,{"disambiguationData":[OSD([sQuery(id+"F3.wireOp",EDGE,"W3A2iIaU-WZcM-LwCZ-avBC-8jkScGPnRnPX"),sQuery(id+"F3.wireOp",EDGE,"ALWewPtL-lRdy-D1S6-Pmp3-0LCmG40DPnmF"),sQuery(id+"F3.wireOp",EDGE,"E269"),sQuery(id+"F3.wireOp",EDGE,"a8HGcZms-0psD-ubHa-zhNr-YMWZytVFjQNi"),sQuery(id+"F3.wireOp",EDGE,"o8Ebxgyn-Q84Y-cI0J-CGKw-LX74F4kokC7l"),sQuery(id+"F3.wireOp",EDGE,"YJE5rnin-kTqy-YI2g-DbKN-iJDOnxPtUyyk"),sQuery(id+"F3.wireOp",EDGE,"J2bwKcV5-MZwX-Vs9f-UurF-KyFTJAMSioa0"),sQuery(id+"F3.wireOp",EDGE,"OojeKQKz-hSKq-U6jK-n3HU-CNnbXeyMiDCb")])],"isStart":true});
            extrude(context, id + "F5", {"entities" : qUnion([Q0]), "operationType" : NewBodyOperationType.ADD, "depth" : 21 * mm, "offsetDistance" : 25 * mm});
        }
        {
            var Q0;
            Q0=makeQuery(id+"F0.imprint","IMPRINT",FACE,{"disambiguationData":[TD([[makeQuery(id+"F0.imprint","IMPRINT",EDGE,{"derivedFrom":sQuery(id+"F0.wireOp",EDGE,"E175")}),1.0]])]});
            var Q1;
            Q1=makeQuery(id+"F0.imprint","IMPRINT",FACE,{"disambiguationData":[TD([[makeQuery(id+"F0.imprint","IMPRINT",EDGE,{"derivedFrom":sQuery(id+"F0.wireOp",EDGE,"E176")}),1.0]])]});
            var Q2;
            Q2=makeQuery(id+"F0.imprint","IMPRINT",FACE,{"disambiguationData":[TD([[makeQuery(id+"F0.imprint","IMPRINT",EDGE,{"derivedFrom":sQuery(id+"F0.wireOp",EDGE,"E172")}),1.0]])]});
            var Q3;
            Q3=makeQuery(id+"F0.imprint","IMPRINT",FACE,{"disambiguationData":[TD([[makeQuery(id+"F0.imprint","IMPRINT",EDGE,{"derivedFrom":sQuery(id+"F0.wireOp",EDGE,"E167")}),1.0]])]});
            var Q4;
            Q4=sQuery(id+"F0.wireOp",EDGE,"E175");
            var Q5;
            Q5=sQuery(id+"F0.wireOp",EDGE,"E176");
            var Q6;
            Q6=sQuery(id+"F0.wireOp",EDGE,"E167");
            var Q7;
            Q7=sQuery(id+"F0.wireOp",EDGE,"E172");
            extrude(context, id + "F6", {"entities" : qUnion([Q0, Q1, Q2, Q3]), "operationType" : NewBodyOperationType.ADD, "surfaceEntities" : qUnion([Q4, Q5, Q6, Q7]), "oppositeDirection" : true, "depth" : 5.5 * mm, "offsetDistance" : 25 * mm});
        }
        {
            var Q0;
            Q0=makeQuery(id+"F0.imprint","IMPRINT",FACE,{"disambiguationData":[TD([[makeQuery(id+"F0.imprint","IMPRINT",EDGE,{"derivedFrom":sQuery(id+"F0.wireOp",EDGE,"E31")}),1.0]])]});
            extrude(context, id + "F7", {"entities" : qUnion([Q0]), "operationType" : NewBodyOperationType.ADD, "oppositeDirection" : true, "depth" : 1.5 * mm, "offsetDistance" : 25 * mm});
        }
        {
            var Q0;
            Q0=makeQuery(id+"F7.opExtrude","CAP_FACE",FACE,{"disambiguationData":[OSD([sQuery(id+"F0.wireOp",EDGE,"E31"),sQuery(id+"F0.wireOp",EDGE,"E34"),sQuery(id+"F0.wireOp",EDGE,"E36"),sQuery(id+"F0.wireOp",EDGE,"E38"),sQuery(id+"F0.wireOp",EDGE,"E39"),sQuery(id+"F0.wireOp",EDGE,"E40"),sQuery(id+"F0.wireOp",EDGE,"E41"),sQuery(id+"F0.wireOp",EDGE,"E42"),sQuery(id+"F0.wireOp",EDGE,"E43"),sQuery(id+"F0.wireOp",EDGE,"E44"),sQuery(id+"F0.wireOp",EDGE,"E45"),sQuery(id+"F0.wireOp",EDGE,"E46"),sQuery(id+"F0.wireOp",EDGE,"E71"),sQuery(id+"F0.wireOp",EDGE,"E72"),sQuery(id+"F0.wireOp",EDGE,"E73"),sQuery(id+"F0.wireOp",EDGE,"E74"),sQuery(id+"F0.wireOp",EDGE,"E75"),sQuery(id+"F0.wireOp",EDGE,"E76"),sQuery(id+"F0.wireOp",EDGE,"E77"),sQuery(id+"F0.wireOp",EDGE,"E78"),sQuery(id+"F0.wireOp",EDGE,"E79"),sQuery(id+"F0.wireOp",EDGE,"E82"),sQuery(id+"F0.wireOp",EDGE,"E83"),sQuery(id+"F0.wireOp",EDGE,"E86"),sQuery(id+"F0.wireOp",EDGE,"E89"),sQuery(id+"F0.wireOp",EDGE,"E90"),sQuery(id+"F0.wireOp",EDGE,"E91"),sQuery(id+"F0.wireOp",EDGE,"E93"),sQuery(id+"F0.wireOp",EDGE,"E213"),sQuery(id+"F0.wireOp",EDGE,"E214"),sQuery(id+"F0.wireOp",EDGE,"E215"),sQuery(id+"F0.wireOp",EDGE,"E216"),sQuery(id+"F0.wireOp",EDGE,"E217"),sQuery(id+"F0.wireOp",EDGE,"E218"),sQuery(id+"F0.wireOp",EDGE,"E219"),sQuery(id+"F0.wireOp",EDGE,"E220"),sQuery(id+"F0.wireOp",EDGE,"E221"),sQuery(id+"F0.wireOp",EDGE,"E226"),sQuery(id+"F0.wireOp",EDGE,"E231"),sQuery(id+"F0.wireOp",EDGE,"E232"),sQuery(id+"F0.wireOp",EDGE,"E249.bottom"),sQuery(id+"F0.wireOp",EDGE,"E249.top"),sQuery(id+"F0.wireOp",EDGE,"E249.left"),sQuery(id+"F0.wireOp",EDGE,"E249.right")])],"isStart":false});
            extrude(context, id + "F8", {"entities" : qUnion([Q0]), "operationType" : NewBodyOperationType.REMOVE, "oppositeDirection" : true, "depth" : 2.5 * mm, "offsetDistance" : 25 * mm});
        }
        {
            var Q0;
            Q0=makeQuery(id+"F0.imprint","IMPRINT",FACE,{"disambiguationData":[TD([[makeQuery(id+"F0.imprint","IMPRINT",EDGE,{"derivedFrom":sQuery(id+"F0.wireOp",EDGE,"E182.bottom")}),-1.0]])]});
            extrude(context, id + "F9", {"entities" : qUnion([Q0]), "operationType" : NewBodyOperationType.ADD, "oppositeDirection" : true, "depth" : 1.5 * mm, "offsetDistance" : 25 * mm});
        }
        {
            var Q0;
            {var subQ0=sQuery(id+"F3.wireOp",EDGE,"E278");var subQ1=sQuery(id+"F3.wireOp",EDGE,"E271");Q0=makeQuery(id+"F9.boolean.opBoolean","MERGE",FACE,{"derivedFrom":[makeQuery(id+"F5.boolean.opBoolean","MERGE",FACE,{"derivedFrom":[makeQuery(id+"F4.opExtrude","SWEPT_FACE",FACE,{"disambiguationData":[OSD([subQ1,subQ0])]}),makeQuery(id+"F5.opExtrude","SWEPT_FACE",FACE,{"disambiguationData":[OSD([subQ1,subQ0])]})]}),makeQuery(id+"F9.opExtrude","CAP_FACE",FACE,{"disambiguationData":[OSD([sQuery(id+"F0.wireOp",EDGE,"E182.bottom"),sQuery(id+"F0.wireOp",EDGE,"E182.top"),sQuery(id+"F0.wireOp",EDGE,"E182.left"),sQuery(id+"F0.wireOp",EDGE,"E182.right"),sQuery(id+"F0.wireOp",EDGE,"E186.trimOffspring"),sQuery(id+"F0.wireOp",EDGE,"E190.trimOffspring"),sQuery(id+"F0.wireOp",EDGE,"E191"),sQuery(id+"F0.wireOp",EDGE,"E192"),sQuery(id+"F0.wireOp",EDGE,"E249.bottom"),sQuery(id+"F0.wireOp",EDGE,"E249.top"),sQuery(id+"F0.wireOp",EDGE,"E249.left"),sQuery(id+"F0.wireOp",EDGE,"E249.right")])],"isStart":false})]});}
            var sketch = newSketch(context, id + "F10", { "sketchPlane" : qUnion([Q0])});
            skPoint(sketch, "E280", {"position": v(0, 19.5) * mm});
            skPoint(sketch, "E281", {"position": v(0, 21) * mm});
            skLineSegment(sketch, "E282", {"start": v(0, 21) * mm, "end": v(21, 21) * mm, "construction": true});
            skLineSegment(sketch, "E283", {"start": v(0, 26.75) * mm, "end": v(0, 25.5) * mm, "construction": true});
            skPoint(sketch, "E284.orphan", {"position": v(-21, 21) * mm});
            skLineSegment(sketch, "E285", {"start": v(0, 21) * mm, "end": v(-21, 21) * mm, "construction": true});
            skLineSegment(sketch, "E286", {"start": v(-10.5, 21) * mm, "end": v(-10.5, 24.25) * mm, "construction": true});
            skLineSegment(sketch, "E287", {"start": v(10.5, 21) * mm, "end": v(10.5, 24.25) * mm, "construction": true});
            skCircle(sketch, "E288", {"center": v(-10.5, 24.25) * mm, "radius": 1.25 * mm});
            skCircle(sketch, "E289", {"center": v(0, 24.25) * mm, "radius": 1.25 * mm});
            skCircle(sketch, "E290", {"center": v(10.5, 24.25) * mm, "radius": 1.25 * mm});
            skPoint(sketch, "E291", {"position": v(-10.5, 25.5) * mm});
            skPoint(sketch, "E292", {"position": v(0, 25.5) * mm});
            skPoint(sketch, "E293", {"position": v(10.5, 25.5) * mm});
            skLineSegment(sketch, "E294.trimOffspring", {"start": v(-10.5, 25.5) * mm, "end": v(-10.5, 26.75) * mm, "construction": true});
            skLineSegment(sketch, "E295.trimOffspring", {"start": v(0, 24.25) * mm, "end": v(0, 21) * mm, "construction": true});
            skLineSegment(sketch, "E296.trimOffspring", {"start": v(10.5, 25.5) * mm, "end": v(10.5, 26.75) * mm, "construction": true});
            skSolve(sketch);
        }
        {
            var Q0;
            Q0=makeQuery(id+"F10.imprint","IMPRINT",FACE,{"disambiguationData":[TD([[makeQuery(id+"F10.imprint","IMPRINT",EDGE,{"derivedFrom":sQuery(id+"F10.wireOp",EDGE,"E290")}),1.0]])]});
            var Q1;
            Q1=makeQuery(id+"F10.imprint","IMPRINT",FACE,{"disambiguationData":[TD([[makeQuery(id+"F10.imprint","IMPRINT",EDGE,{"derivedFrom":sQuery(id+"F10.wireOp",EDGE,"E289")}),1.0]])]});
            var Q2;
            Q2=makeQuery(id+"F10.imprint","IMPRINT",FACE,{"disambiguationData":[TD([[makeQuery(id+"F10.imprint","IMPRINT",EDGE,{"derivedFrom":sQuery(id+"F10.wireOp",EDGE,"E288")}),1.0]])]});
            var Q3;
            Q3=sQuery(id+"F10.wireOp",EDGE,"E288");
            var Q4;
            Q4=sQuery(id+"F10.wireOp",EDGE,"E289");
            var Q5;
            Q5=sQuery(id+"F10.wireOp",EDGE,"E290");
            extrude(context, id + "F11", {"entities" : qUnion([Q0, Q1, Q2]), "operationType" : NewBodyOperationType.REMOVE, "surfaceEntities" : qUnion([Q3, Q4, Q5]), "oppositeDirection" : true, "depth" : 2.5 * mm, "offsetDistance" : 25 * mm});
        }
        {
            var Q0;
            Q0=makeQuery(id+"F0.imprint","IMPRINT",FACE,{"disambiguationData":[TD([[makeQuery(id+"F0.imprint","IMPRINT",EDGE,{"derivedFrom":sQuery(id+"F0.wireOp",EDGE,"E263")}),1.0]])]});
            var Q1;
            Q1=makeQuery(id+"F0.imprint","IMPRINT",FACE,{"disambiguationData":[TD([[makeQuery(id+"F0.imprint","IMPRINT",EDGE,{"derivedFrom":sQuery(id+"F0.wireOp",EDGE,"E255")}),-1.0]])]});
            extrude(context, id + "F12", {"entities" : qUnion([Q0, Q1]), "operationType" : NewBodyOperationType.REMOVE, "depth" : 5 * mm, "offsetDistance" : 25 * mm});
        }
        {
            var Q0;
            Q0=makeQuery(id+"F0.imprint","IMPRINT",FACE,{"disambiguationData":[TD([[makeQuery(id+"F0.imprint","IMPRINT",EDGE,{"derivedFrom":sQuery(id+"F0.wireOp",EDGE,"E32")}),-1.0]])]});
            extrude(context, id + "F13", {"entities" : qUnion([Q0]), "operationType" : NewBodyOperationType.REMOVE, "depth" : 1 * mm, "offsetDistance" : 25 * mm});
        }
    });
